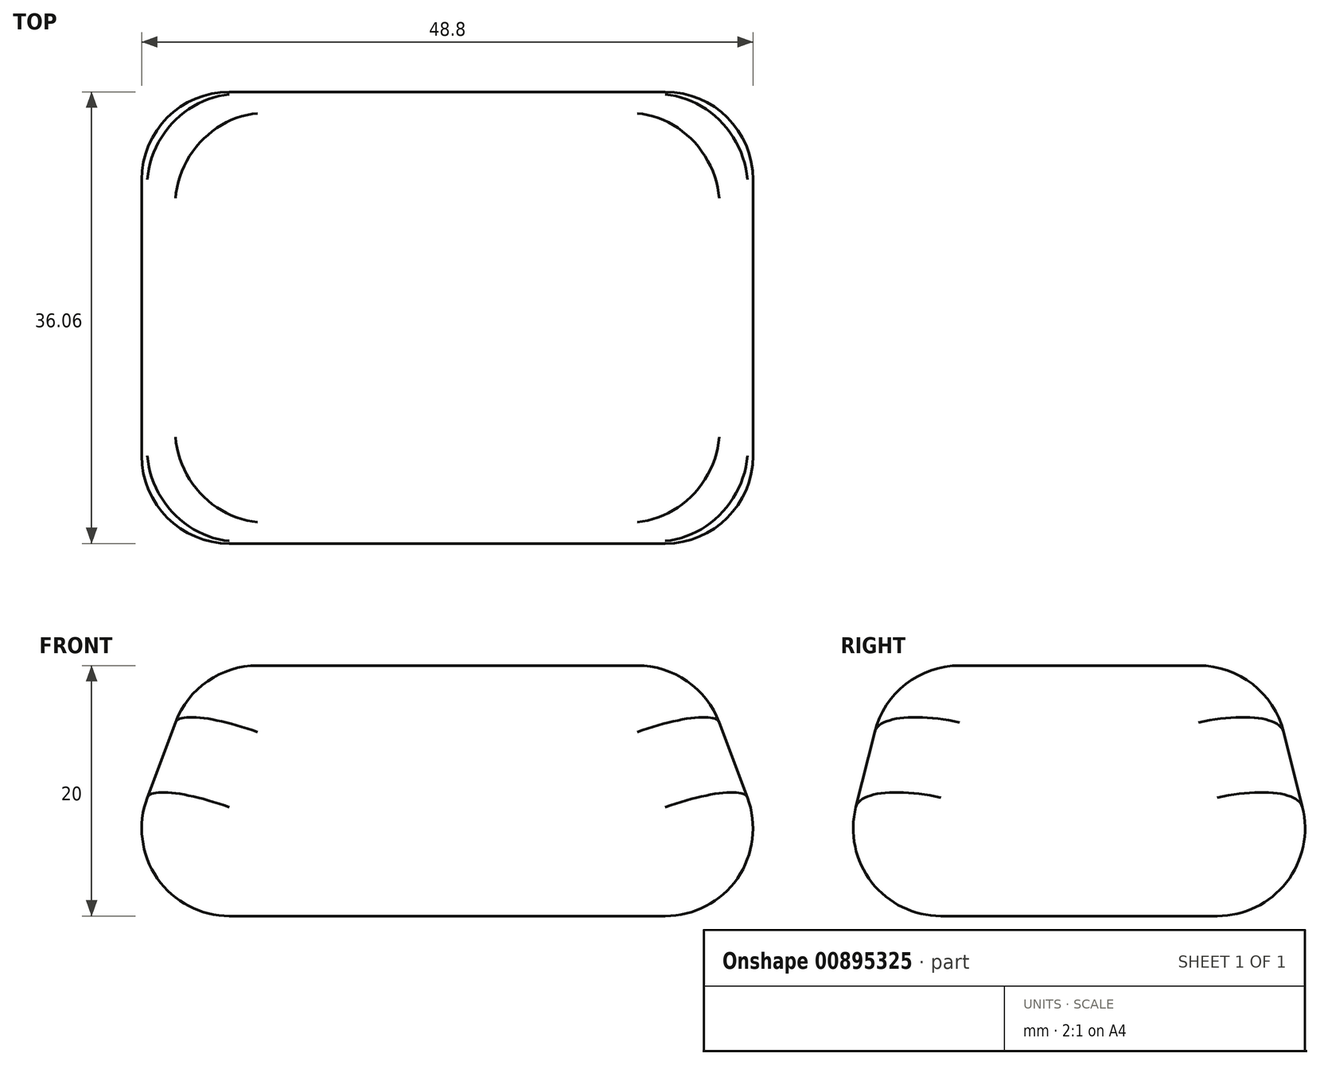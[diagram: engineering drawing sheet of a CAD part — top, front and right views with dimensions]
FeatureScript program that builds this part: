
annotation { "Feature Type Name" : "Feature", "Feature Type Description" : "" }
export const myFeature = defineFeature(function(context is Context, id is Id, definition is map)
    precondition{}
    {
        {
            var Q0;
            Q0=qCreatedBy(makeId("Top.planeOp"),FACE);
            var sketch = newSketch(context, id + "F0", { "sketchPlane" : qUnion([Q0])});
            skLineSegment(sketch, "E0.bottom", {"start": v(27.5, -20) * mm, "end": v(-27.5, -20) * mm});
            skLineSegment(sketch, "E0.top", {"start": v(27.5, 20) * mm, "end": v(-27.5, 20) * mm});
            skLineSegment(sketch, "E0.left", {"start": v(27.5, -20) * mm, "end": v(27.5, 20) * mm});
            skLineSegment(sketch, "E0.right", {"start": v(-27.5, -20) * mm, "end": v(-27.5, 20) * mm});
            skPoint(sketch, "E0.middle", {"position": v(0, 0) * mm});
            skSolve(sketch);
        }
        {
            var Q0;
            Q0=qCreatedBy(makeId("Top.planeOp"),FACE);
            cPlane(context, id + "F1", {"entities" : qUnion([Q0]), "cplaneType" : CPlaneType.OFFSET, "offset" : 20 * mm, "width" : 150 * mm, "height" : 150 * mm});
        }
        {
            var Q0;
            Q0=qCreatedBy(id+"F1.planeOp",FACE);
            var sketch = newSketch(context, id + "F2", { "sketchPlane" : qUnion([Q0])});
            skLineSegment(sketch, "E1.bottom", {"start": v(20, -15) * mm, "end": v(-20, -15) * mm});
            skLineSegment(sketch, "E1.top", {"start": v(20, 15) * mm, "end": v(-20, 15) * mm});
            skLineSegment(sketch, "E1.left", {"start": v(20, -15) * mm, "end": v(20, 15) * mm});
            skLineSegment(sketch, "E1.right", {"start": v(-20, -15) * mm, "end": v(-20, 15) * mm});
            skPoint(sketch, "E1.middle", {"position": v(0, 0) * mm});
            skSolve(sketch);
        }
        {
            var Q0;
            Q0=makeQuery(id+"F0.imprint","IMPRINT",FACE,{"disambiguationData":[TD([[makeQuery(id+"F0.imprint","IMPRINT",EDGE,{"derivedFrom":sQuery(id+"F0.wireOp",EDGE,"E0.bottom")}),-1.0]])]});
            var Q1;
            Q1=makeQuery(id+"F2.imprint","IMPRINT",FACE,{"disambiguationData":[TD([[makeQuery(id+"F2.imprint","IMPRINT",EDGE,{"derivedFrom":sQuery(id+"F2.wireOp",EDGE,"E1.bottom")}),-1.0]])]});
            loft(context, id + "F3", {"sheetProfilesArray" : [{ "sheetProfileEntities" : qUnion([Q0]) }, { "sheetProfileEntities" : qUnion([Q1]) }]});
        }
        {
            var Q0;
            Q0=makeQuery(id+"F3.opLoft","SWEPT_EDGE",EDGE,{"disambiguationData":[OSD([sQuery(id+"F0.wireOp",EDGE,"E0.bottom"),sQuery(id+"F0.wireOp",EDGE,"E0.left"),sQuery(id+"F2.wireOp",EDGE,"E1.bottom"),sQuery(id+"F2.wireOp",EDGE,"E1.left")])]});
            var Q1;
            Q1=makeQuery(id+"F3.opLoft","SWEPT_EDGE",EDGE,{"disambiguationData":[OSD([sQuery(id+"F0.wireOp",EDGE,"E0.top"),sQuery(id+"F0.wireOp",EDGE,"E0.left"),sQuery(id+"F2.wireOp",EDGE,"E1.top"),sQuery(id+"F2.wireOp",EDGE,"E1.left")])]});
            var Q2;
            Q2=makeQuery(id+"F3.opLoft","SWEPT_EDGE",EDGE,{"disambiguationData":[OSD([sQuery(id+"F0.wireOp",EDGE,"E0.top"),sQuery(id+"F0.wireOp",EDGE,"E0.right"),sQuery(id+"F2.wireOp",EDGE,"E1.top"),sQuery(id+"F2.wireOp",EDGE,"E1.right")])]});
            var Q3;
            Q3=makeQuery(id+"F3.opLoft","SWEPT_EDGE",EDGE,{"disambiguationData":[OSD([sQuery(id+"F0.wireOp",EDGE,"E0.bottom"),sQuery(id+"F0.wireOp",EDGE,"E0.right"),sQuery(id+"F2.wireOp",EDGE,"E1.bottom"),sQuery(id+"F2.wireOp",EDGE,"E1.right")])]});
            var Q4;
            Q4=makeQuery(id+"F3.opLoft","MID_CAP_EDGE",EDGE,{"disambiguationData":[OSD([sQuery(id+"F2.wireOp",EDGE,"E1.bottom"),sQuery(id+"F2.wireOp",EDGE,"E1.top"),sQuery(id+"F2.wireOp",EDGE,"E1.right")])],"capPos":1.0});
            var Q5;
            Q5=makeQuery(id+"F3.opLoft","MID_CAP_EDGE",EDGE,{"disambiguationData":[OSD([sQuery(id+"F0.wireOp",EDGE,"E0.bottom"),sQuery(id+"F0.wireOp",EDGE,"E0.top"),sQuery(id+"F0.wireOp",EDGE,"E0.right")])],"capPos":0.0});
            var Q6;
            Q6=makeQuery(id+"F3.opLoft","MID_CAP_EDGE",EDGE,{"disambiguationData":[OSD([sQuery(id+"F0.wireOp",EDGE,"E0.bottom"),sQuery(id+"F0.wireOp",EDGE,"E0.left"),sQuery(id+"F0.wireOp",EDGE,"E0.right")])],"capPos":0.0});
            var Q7;
            Q7=makeQuery(id+"F3.opLoft","CAP_FACE",FACE,{"disambiguationData":[OSD([makeQuery(id+"F0.imprint","IMPRINT",FACE,{"disambiguationData":[TD([[makeQuery(id+"F0.imprint","IMPRINT",EDGE,{"derivedFrom":sQuery(id+"F0.wireOp",EDGE,"E0.bottom")}),-1.0]])]})])],"isStart":true});
            var Q8;
            Q8=makeQuery(id+"F3.opLoft","CAP_FACE",FACE,{"disambiguationData":[OSD([makeQuery(id+"F2.imprint","IMPRINT",FACE,{"disambiguationData":[TD([[makeQuery(id+"F2.imprint","IMPRINT",EDGE,{"derivedFrom":sQuery(id+"F2.wireOp",EDGE,"E1.bottom")}),-1.0]])]})])],"isStart":true});
            fillet(context, id + "F4", {"entities" : qUnion([Q0, Q1, Q2, Q3, Q4, Q5, Q6, Q7, Q8]), "radius" : 7 * mm, "tangentPropagation" : true, "allowEdgeOverflow" : false});
        }
    });
